# Revit family: CDS-0
name_source: partatom
category: Air Terminals
revit_build: Autodesk Revit MEP 2012 (Build: 20110309_2315(x64)
units: mm (PartAtom-declared; Revit-internal decimal feet)

## types (12) — shared parameters
Altura A = 19 3/8"
Altura perfil = 5/8"
Altura tapa = 19 1/2"
Cuello = Redondo
Diametro = 5 7/8"
Diametro espesor saliente = 6"
Manufacturer = INNES
Máxima presión estática = 0.00 in-wg
Máxima velocidad de cuello = 0 FPM
Mínima presión estática = 0.00 in-wg
Mínima velocidad de cuello = 0 FPM
URL = http://www.innes.com.mx

## per-type parameters (varying)
| type | Ancho C | Ancho base C | Caja derecha | Caja izquierda | Espesor B | Espesor C | Largo B | Largo base B | Radio | Radio ext |
| CDS-0-I-06 | 12" | 10 3/4" | No | Yes | 7 7/8" | 11 7/8" | 8" | 6 3/4" | 2 15/16" | 3 1/16" |
| CDS-0-I-08 | 12" | 10 3/4" | No | Yes | 9 7/8" | 11 7/8" | 10" | 8 3/4" | 3 15/16" | 4 1/16" |
| CDS-0-I-10 | 14" | 12 3/4" | No | Yes | 12 3/8" | 13 7/8" | 12 1/2" | 11 1/4" | 4 15/16" | 5 1/16" |
| CDS-0-I-16 | 24" | 22 3/4" | No | Yes | 17 7/8" | 23 7/8" | 18" | 16 3/4" | 7 15/16" | 8 1/16" |
| CDS-0-D-06 | 12" | 10 3/4" | Yes | No | 7 7/8" | 11 7/8" | 8" | 6 3/4" | 2 15/16" | 3 1/16" |
| CDS-0-D-08 | 12" | 10 3/4" | Yes | No | 9 7/8" | 11 7/8" | 10" | 8 3/4" | 3 15/16" | 4 1/16" |
| CDS-0-D-10 | 14" | 12 3/4" | Yes | No | 12 3/8" | 13 7/8" | 12 1/2" | 11 1/4" | 4 15/16" | 5 1/16" |
| CDS-0-D-16 | 24" | 22 3/4" | Yes | No | 17 7/8" | 23 7/8" | 18" | 16 3/4" | 7 15/16" | 8 1/16" |
| CDS-0-S-06 | 12" | 10 3/4" | No | No | 7 7/8" | 11 7/8" | 8" | 6 3/4" | 2 15/16" | 3 1/16" |
| CDS-0-S-08 | 12" | 10 3/4" | No | No | 9 7/8" | 11 7/8" | 10" | 8 3/4" | 3 15/16" | 4 1/16" |
| CDS-0-S-10 | 14" | 12 3/4" | No | No | 12 3/8" | 13 7/8" | 12 1/2" | 11 1/4" | 4 15/16" | 5 1/16" |
| CDS-0-S-16 | 24" | 22 3/4" | No | No | 17 7/8" | 23 7/8" | 18" | 16 3/4" | 7 15/16" | 8 1/16" |

## geometry (parser evidence)
native form markers: Sweep x1
no freeform markers — native parametric forms only
